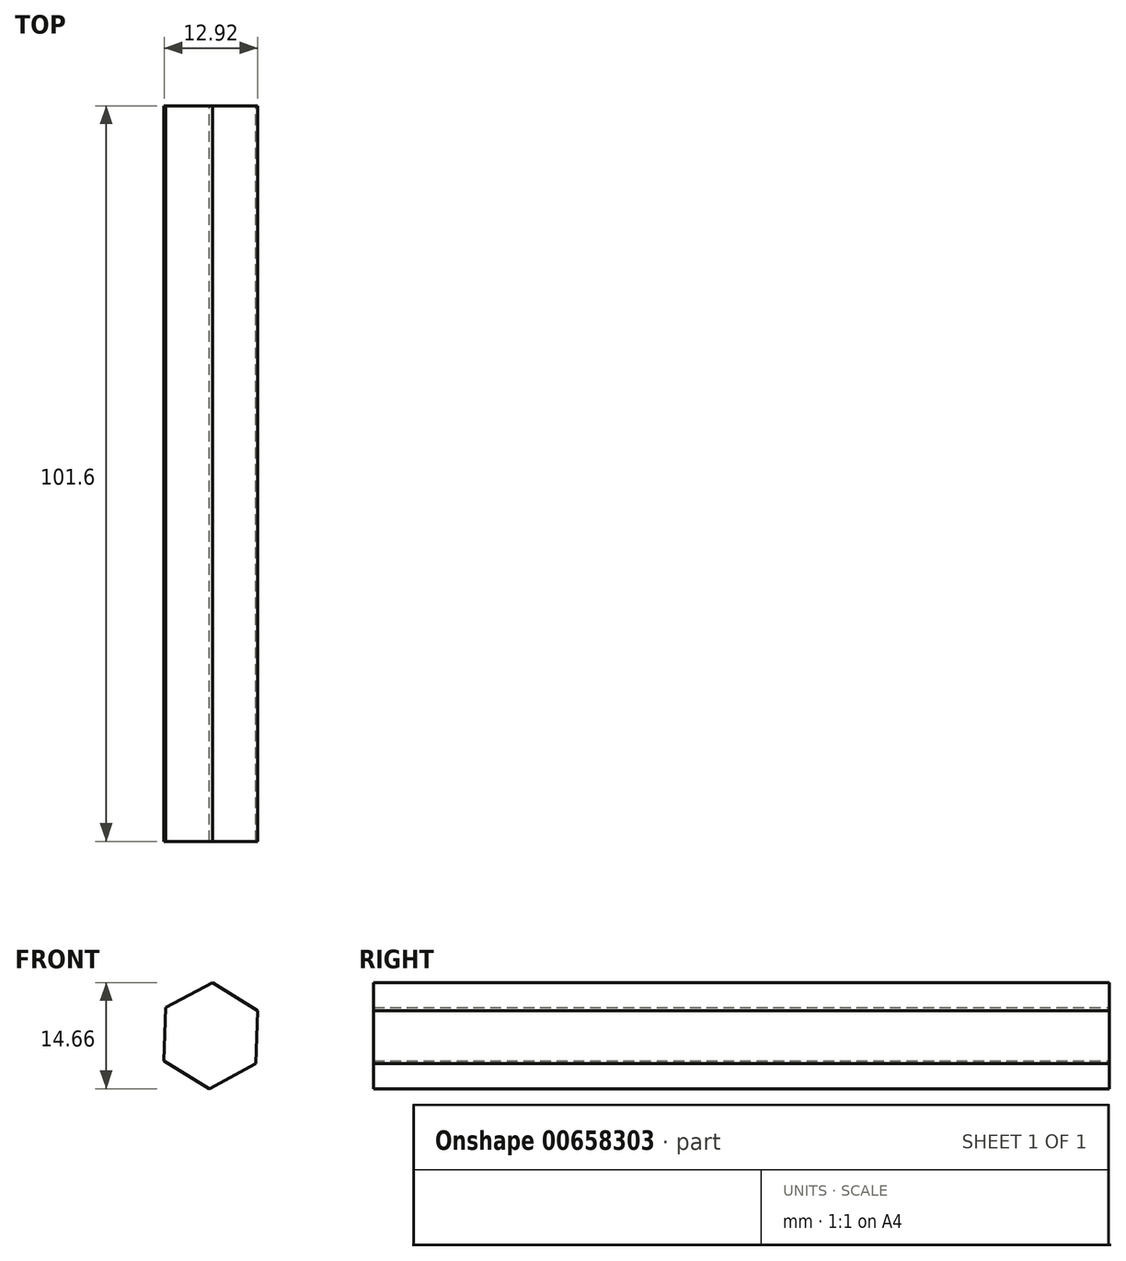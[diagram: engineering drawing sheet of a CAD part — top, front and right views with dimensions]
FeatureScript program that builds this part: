
annotation { "Feature Type Name" : "Feature", "Feature Type Description" : "" }
export const myFeature = defineFeature(function(context is Context, id is Id, definition is map)
    precondition{}
    {
        {
            var Q0;
            Q0=qCreatedBy(makeId("Front.planeOp"),FACE);
            var sketch = newSketch(context, id + "F0", { "sketchPlane" : qUnion([Q0])});
            skCircle(sketch, "E0", {"center": v(0, 0) * mm, "radius": 6.35 * mm});
            skSolve(sketch);
        }
        {
            var Q0;
            Q0 = qSketchRegion(id + "F0", true);
            extrude(context, id + "F1", {"entities" : qUnion([Q0]), "depth" : 101.6 * mm, "offsetDistance" : 25.4 * mm});
        }
        {
            var Q0;
            Q0=qCreatedBy(makeId("Front.planeOp"),FACE);
            var sketch = newSketch(context, id + "F2", { "sketchPlane" : qUnion([Q0])});
            skCircle(sketch, "E1.cCircle", {"center": v(0, 0) * mm, "radius": 7.33 * mm, "construction": true});
            skLineSegment(sketch, "E1.0", {"start": v(-6.46, -3.46) * mm, "end": v(-6.23, 3.87) * mm});
            skLineSegment(sketch, "E1.1", {"start": v(-6.23, 3.87) * mm, "end": v(0.23, 7.33) * mm});
            skLineSegment(sketch, "E1.2", {"start": v(0.23, 7.33) * mm, "end": v(6.46, 3.46) * mm});
            skLineSegment(sketch, "E1.3", {"start": v(6.46, 3.46) * mm, "end": v(6.23, -3.87) * mm});
            skLineSegment(sketch, "E1.4", {"start": v(6.23, -3.87) * mm, "end": v(-0.23, -7.33) * mm});
            skLineSegment(sketch, "E1.5", {"start": v(-0.23, -7.33) * mm, "end": v(-6.46, -3.46) * mm});
            skSolve(sketch);
        }
        {
            var Q0;
            Q0 = qSketchRegion(id + "F2", true);
            extrude(context, id + "F3", {"entities" : qUnion([Q0]), "operationType" : NewBodyOperationType.ADD, "depth" : 101.6 * mm, "offsetDistance" : 25.4 * mm});
        }
    });
